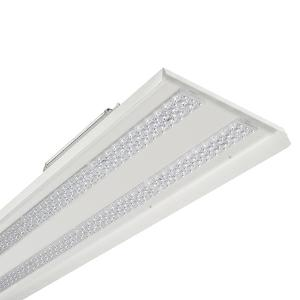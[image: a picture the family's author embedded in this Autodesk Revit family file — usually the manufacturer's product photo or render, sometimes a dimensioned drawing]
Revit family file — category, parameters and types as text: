
# Revit family: 3f_filippi_-_kit_led_retrofit_beta_430_2x_3f_filippi_-_a5309_a5322_-_kit_led_beta_430_-_l1551-_2x65w_conc___vs_4a64
name_source: partatom
category: Lighting Fixtures
units: mm (PartAtom-declared; Revit-internal decimal feet)

## family parameters
Cut with Voids When Loaded = No
Host = Face
Light Source = No
Part Type = Normal
Room Calculation Point = No
Round Connector Dimension = Use Diameter
Shared = No

## types (1)
- 3F Filippi - Kit LED Retrofit Beta 430 2X (1 x LED, 16724 lm, 120 W, 4000 K)
    Apparent Load = 120 VA
    Approval mark = ENEC
    CIE Flux Codes = 73 92 98 100 100
    Color Rendering = 80
    Color Temperature = 4000 K
    Control Gear = Electronic ballast
    Default Elevation = 1800 mm
    Description = Beta 430 Retrofit Kit to replace the 4x49W T5 Amalgam or the 4x58W T8 version

ILLUMINOTECHNICAL
Luminous efficiency 100% (DLOR 100%, ULOR 0%).
Initial luminous flux of the luminaire 16724 lm.
Symmetric concentrated distribution.
Installation Interdistance Transv.D = 0.63 x hu - Long.D = 0.95 x hu.
Tabular UGR (CIE 117 - 4H-8H; S=0.25H; 70/50/20): RUG 18 - 19.2.
Beam angle: 40° - 65°.
Luminous efficacy 139 lm/W.
Lifetime (L93/B10): 30000 h. (tq+25°C)
Lifetime (L90/B10): 50000 h. (tq+25°C)
Lifetime (L85/B10): 80000 h. (tq+25°C)
Lifetime (L80/B10): 100000 h. (tq+25°C)
Lifetime (L85/B10): 50000 h. (tq+40°C)
Sudden decreased luminous flux after 50000 hours: 0% (C0).
Photobiological safety in compliance with IEC/TR 62778: RG0 risk exempt, (IEC 62471).
In compliance with IEC/EN 62722-2-1 - IEC/EN 62717 standards.

SOURCE
2 linear LED modules 65W/840.
Energy efficiency class (UE 2019/2020 - UE 2019/2015): C.
CIE 13.3 Colour rendering index: CRI >80 (R9 <50%).
IES TM-30 Fidelity Index: Rf = 84 Rg = 95.
CCT nominal colour temperature 4000 K.
Colour initial tolerance (MacAdam): SDCM 3.

MECHANICAL
Gear-tray unit hot-galvanised steel, painted in white polyester.
Methacrylate (PMMA) lenses with external flat surface.
Luminaire with limited surface temperature. - D - (EN 60598-2-24)
Dimensions: 1551x430 mm, height 159 mm. Weight 12.65 kg.
Mechanical strength to impacts IK08 (5 joule).
Glow-wire test resistance 850°C.

ELECTRICAL
Halogen Free electronic wiring 230V-50/60Hz, power factor 0.97, THD <25%, constant output current, class I, 2 driver.
Twin-circuit.
Power of the luminaire 120 W.
CE - IEC 60598-1 - EN 60598-1.
SAFE FLICKER: PstLM=<1 and SVM=<0.4 (IEC TR 61547-1 and IEC TR 63158), to ensure a more comfortable and safe light.
Luminaire compliant with EN 60598-2-22 for power supply from a centralised emergency system CPSS (Central Power Supply System), not incorporated in the luminaire - high risk areas excluded. The default power and flux are 100% in AC and 100% in DC.
Ambient temperature from -20°C to +40°C.
Temperature class T6 max 85°C.
Relative humidity UR: <85%.

INSTALLATION
Retrofit.
Correct installation of the retrofit LED kit, compliant with EN 60598-1 and CE marked, inside the 3F Filippi - Beta 4x and 6x i3F 76 Fluorescent luminaires must be only carried out by qualified personnel to ensure compliance with the national installation standards.
Attention: to maintain the degree of protection of the device and for the purposes of validity of the guarantee of the new retrofit kits, it is imperative to replace the old cable guides (on the body of the device) with the new ones supplied.
All accessories dedicated to this product are available on the Catalog and on our website www.3F-Filippi.com.

ACCESSORIES
A5322 - Printed glass with Beta 430 frame - L1551.

WARNING
Fixture not suitable for cold stores with an ambient temperature <0°C and/or relative humidity >85%.
Luminaire designed for disposal/recycling at end-of-life.
Replaceable (LED only) light source by a professional. Replaceable control gear by a professional.
    Height = 159 mm
    Lamp = 1 x LED
    Lamp Light Flux = 16724 lm
    Lamp Power = 120 W
    Lamp count = 1
    Length = 1551 mm
    Lifetime = 50000 h
    Luminous efficacy = 139 lm/W
    Manufacturer = 3F Filippi
    ModVariant = No
    Model = 3F Filippi - A5309+A5322 - Kit LED Beta 430 - L1551- 2X65W CONC + VS
    Mounting Place = Ceiling
    Mounting Type = Surface mounted
    Number of Poles = 1
    OnlyDefault = Yes
    Power Factor = 1
    Product Name = 3F Filippi - Kit LED Retrofit Beta 430 2X
    Product group = ceiling mounted luminaire
    ProductGroupID = 3
    Protection Class = Protection class I
    Protection Degree = Degree of protection
    RLX_Detail_Level = 1
    RLX_Emergency_Light_Flux = 0 lm
    RLX_Emergency_Type = 0
    RLX_Emergency_Type_DB = No
    RlxData = <blob elided: 69685 chars, md5=8350c95b>
    Socket = socket
    Standby Power = 0 W
    System Light Flux = 16724 lm
    System Power = 120 W
    Type Comments = Product without accessories
    Type Image = 3ffilippi_a5309_a5322.jpg
    URL = http://relux.com
    VarID = ---
    Voltage = 0 V
    Weight = 0.00 kg
    Width = 430 mm

## geometry (parser evidence)
native form markers: Blend x4, Sweep x10
no freeform markers — native parametric forms only
